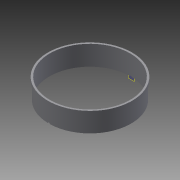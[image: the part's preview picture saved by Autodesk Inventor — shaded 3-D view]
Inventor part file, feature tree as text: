
AUTODESK INVENTOR PART (.ipt)
format: ipt  version: 2015 (Build 190159000, 159)  size: 123,392 bytes
history: native  units: in
note: dims shown in document units (in); Inventor stores cm internally (conversion verified against a paired STEP export)
features: sketch x2, revolve x1, plane x1, hole x1
ambient origin geometry x8: Origin, YZ Plane, XZ Plane, XY Plane, X Axis, Y Axis, Z Axis, Center Point
bodies: Solid1 (feature_tree)
feature tree (5):
  revolve  "Revolution1"  Angle=90.0deg
  plane  "Work Plane1"
  hole  "Hole1"  [1 undecoded]
  sketch  "Sketch1"  dims[d0=1.25in d1=0.125in d2=1.125in d3=4.375in d4=0.125in d5=5.75in d6=0.125in d7=0.5in d8=1.625in d9=0.125in d10=90.0deg]
  sketch  "Sketch2"  dims[d11=0.275in d12=0.75in d13=0.375in d14=0.25in d15=0.5635in d16=1.0in d17=0.8108in]
note: 1 required parameter value undecoded (feature->parameter linkage not recoverable at this tier; creation-order binding heuristic only, values carry confidence <= 0.55)
